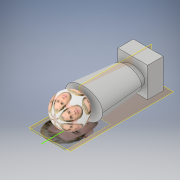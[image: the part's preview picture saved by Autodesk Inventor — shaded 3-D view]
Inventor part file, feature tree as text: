
AUTODESK INVENTOR PART (.ipt)
format: ipt  version: 2017 (Build 210142000, 142)  size: 319,488 bytes
history: native  units: in
note: dims shown in document units (in); Inventor stores cm internally (conversion verified against a paired STEP export)
features: sketch x6, extrude x4, projected_geometry x3, plane x2, revolve x1, other x1
ambient origin geometry x8: Origin, YZ Plane, XZ Plane, XY Plane, X Axis, Y Axis, Z Axis, Center Point
bodies: Solid1 (feature_tree)
feature tree (17):
  extrude  "Extrusion1"  Depth=0.575in
  extrude  "Extrusion2"  Depth=0.236in
  extrude  "Extrusion3"  Depth=0.115in TaperAngle=0.0deg
  plane  "Work Plane1"
  extrude  "Extrusion4"  Depth=0.84in
  revolve  "Revolution2"  Angle=90.0deg
  plane  "Work Plane2"
  sketch  "Sketch7"
  sketch  "Sketch1"  dims[d0=0.575in d1=0.575in]
  sketch  "Sketch2"  dims[d2=0.3in d3=0.0in d4=0.236in]
  sketch  "Sketch3"  dims[d5=0.155in d6=0.115in d7=0.0in]
  sketch  "Sketch4"  dims[d8=0.05in d9=0.84in d10=0.0344in]
  projected_geometry  "Projected Loop1"
  projected_geometry  "Projected Loop2"
  sketch  "Sketch6"  dims[d12=0.84in d13=0.0in d18=90.0deg]
  projected_geometry  "Projected Loop4"
  other  "Image1"
